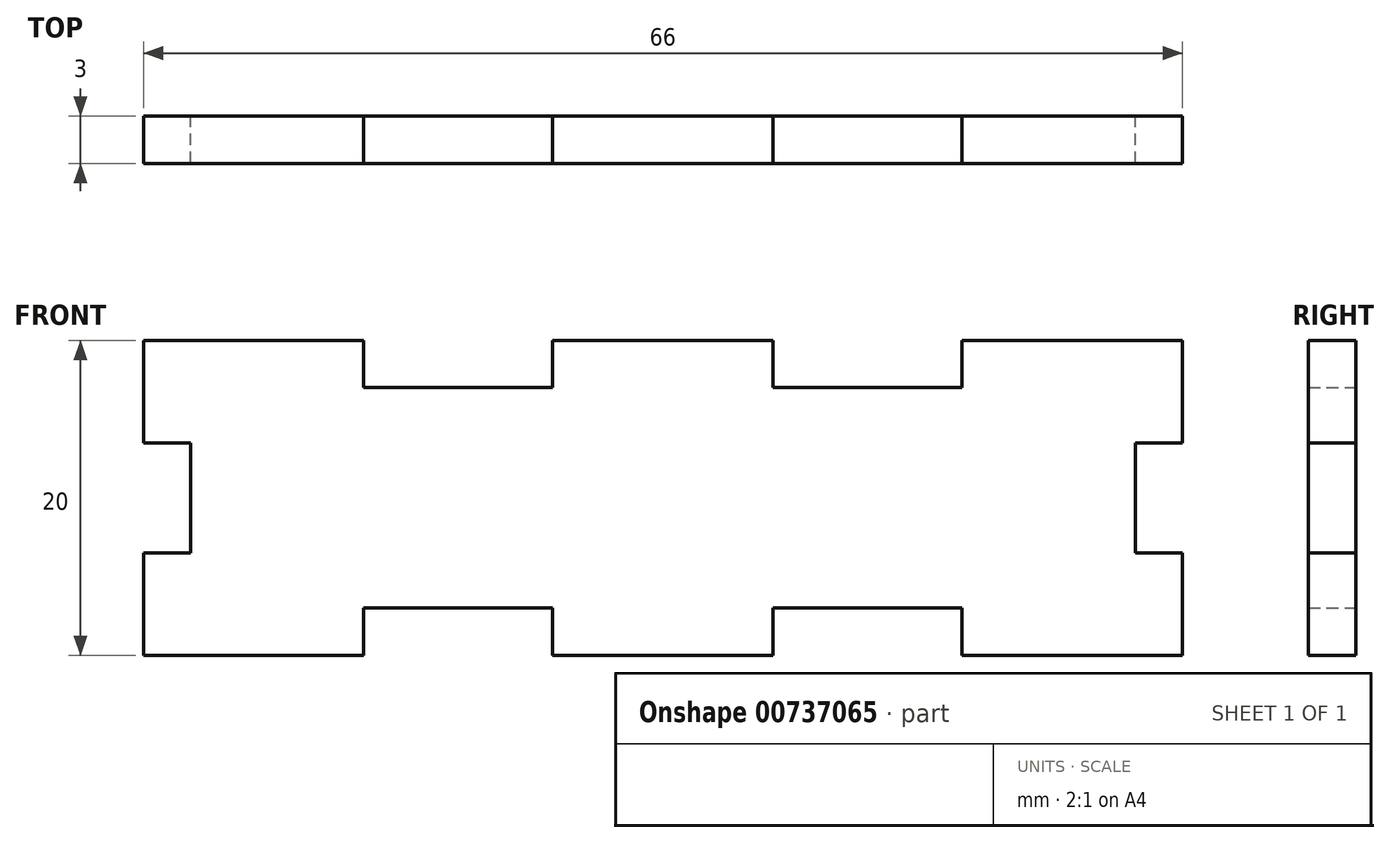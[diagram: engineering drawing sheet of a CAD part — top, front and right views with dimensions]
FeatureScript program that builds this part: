
annotation { "Feature Type Name" : "Feature", "Feature Type Description" : "" }
export const myFeature = defineFeature(function(context is Context, id is Id, definition is map)
    precondition{}
    {
        {
            var Q0;
            Q0=qCreatedBy(makeId("Front.planeOp"),FACE);
            var sketch = newSketch(context, id + "F0", { "sketchPlane" : qUnion([Q0])});
            skLineSegment(sketch, "E0.bottom", {"start": v(33, -10) * mm, "end": v(-33, -10) * mm, "construction": true});
            skLineSegment(sketch, "E0.top", {"start": v(33, 10) * mm, "end": v(-33, 10) * mm, "construction": true});
            skLineSegment(sketch, "E0.left", {"start": v(33, -10) * mm, "end": v(33, 10) * mm, "construction": true});
            skLineSegment(sketch, "E0.right", {"start": v(-33, -10) * mm, "end": v(-33, 10) * mm, "construction": true});
            skPoint(sketch, "E0.middle", {"position": v(0, 0) * mm});
            skLineSegment(sketch, "E1", {"start": v(-33, 10) * mm, "end": v(-19, 10) * mm});
            skLineSegment(sketch, "E2", {"start": v(-19, 10) * mm, "end": v(-19, 7) * mm});
            skLineSegment(sketch, "E3", {"start": v(-19, 7) * mm, "end": v(-7, 7) * mm});
            skLineSegment(sketch, "E4", {"start": v(-7, 7) * mm, "end": v(-7, 10) * mm});
            skLineSegment(sketch, "E5", {"start": v(-7, 10) * mm, "end": v(7, 10) * mm});
            skLineSegment(sketch, "E6", {"start": v(7, 10) * mm, "end": v(7, 7) * mm});
            skLineSegment(sketch, "E7", {"start": v(7, 7) * mm, "end": v(19, 7) * mm});
            skLineSegment(sketch, "E8", {"start": v(19, 7) * mm, "end": v(19, 10) * mm});
            skLineSegment(sketch, "E9", {"start": v(19, 10) * mm, "end": v(33, 10) * mm});
            skLineSegment(sketch, "E10", {"start": v(33, -10) * mm, "end": v(19, -10) * mm});
            skLineSegment(sketch, "E11", {"start": v(19, -10) * mm, "end": v(19, -7) * mm});
            skLineSegment(sketch, "E12", {"start": v(19, -7) * mm, "end": v(7, -7) * mm});
            skLineSegment(sketch, "E13", {"start": v(7, -7) * mm, "end": v(7, -10) * mm});
            skLineSegment(sketch, "E14", {"start": v(7, -10) * mm, "end": v(-7, -10) * mm});
            skLineSegment(sketch, "E15", {"start": v(-7, -10) * mm, "end": v(-7, -7) * mm});
            skLineSegment(sketch, "E16", {"start": v(-7, -7) * mm, "end": v(-19, -7) * mm});
            skLineSegment(sketch, "E17", {"start": v(-19, -7) * mm, "end": v(-19, -10) * mm});
            skLineSegment(sketch, "E18", {"start": v(-19, -10) * mm, "end": v(-33, -10) * mm});
            skLineSegment(sketch, "E19", {"start": v(-33, 10) * mm, "end": v(-33, 3.5) * mm});
            skLineSegment(sketch, "E20", {"start": v(-33, 3.5) * mm, "end": v(-30, 3.5) * mm});
            skLineSegment(sketch, "E21", {"start": v(-30, 3.5) * mm, "end": v(-30, -3.5) * mm});
            skLineSegment(sketch, "E22", {"start": v(-30, -3.5) * mm, "end": v(-33, -3.5) * mm});
            skLineSegment(sketch, "E23", {"start": v(-33, -3.5) * mm, "end": v(-33, -10) * mm});
            skLineSegment(sketch, "E24", {"start": v(33, 10) * mm, "end": v(33, 3.5) * mm});
            skLineSegment(sketch, "E25", {"start": v(33, 3.5) * mm, "end": v(30, 3.5) * mm});
            skLineSegment(sketch, "E26", {"start": v(30, 3.5) * mm, "end": v(30, -3.5) * mm});
            skLineSegment(sketch, "E27", {"start": v(30, -3.5) * mm, "end": v(33, -3.5) * mm});
            skLineSegment(sketch, "E28", {"start": v(33, -3.5) * mm, "end": v(33, -10) * mm});
            skSolve(sketch);
        }
        {
            var Q0;
            Q0=makeQuery(id+"F0.imprint","IMPRINT",FACE,{"disambiguationData":[TD([[makeQuery(id+"F0.imprint","IMPRINT",EDGE,{"derivedFrom":sQuery(id+"F0.wireOp",EDGE,"E1")}),-1.0]])]});
            extrude(context, id + "F1", {"entities" : qUnion([Q0]), "depth" : 3 * mm, "offsetDistance" : 25 * mm});
        }
    });
